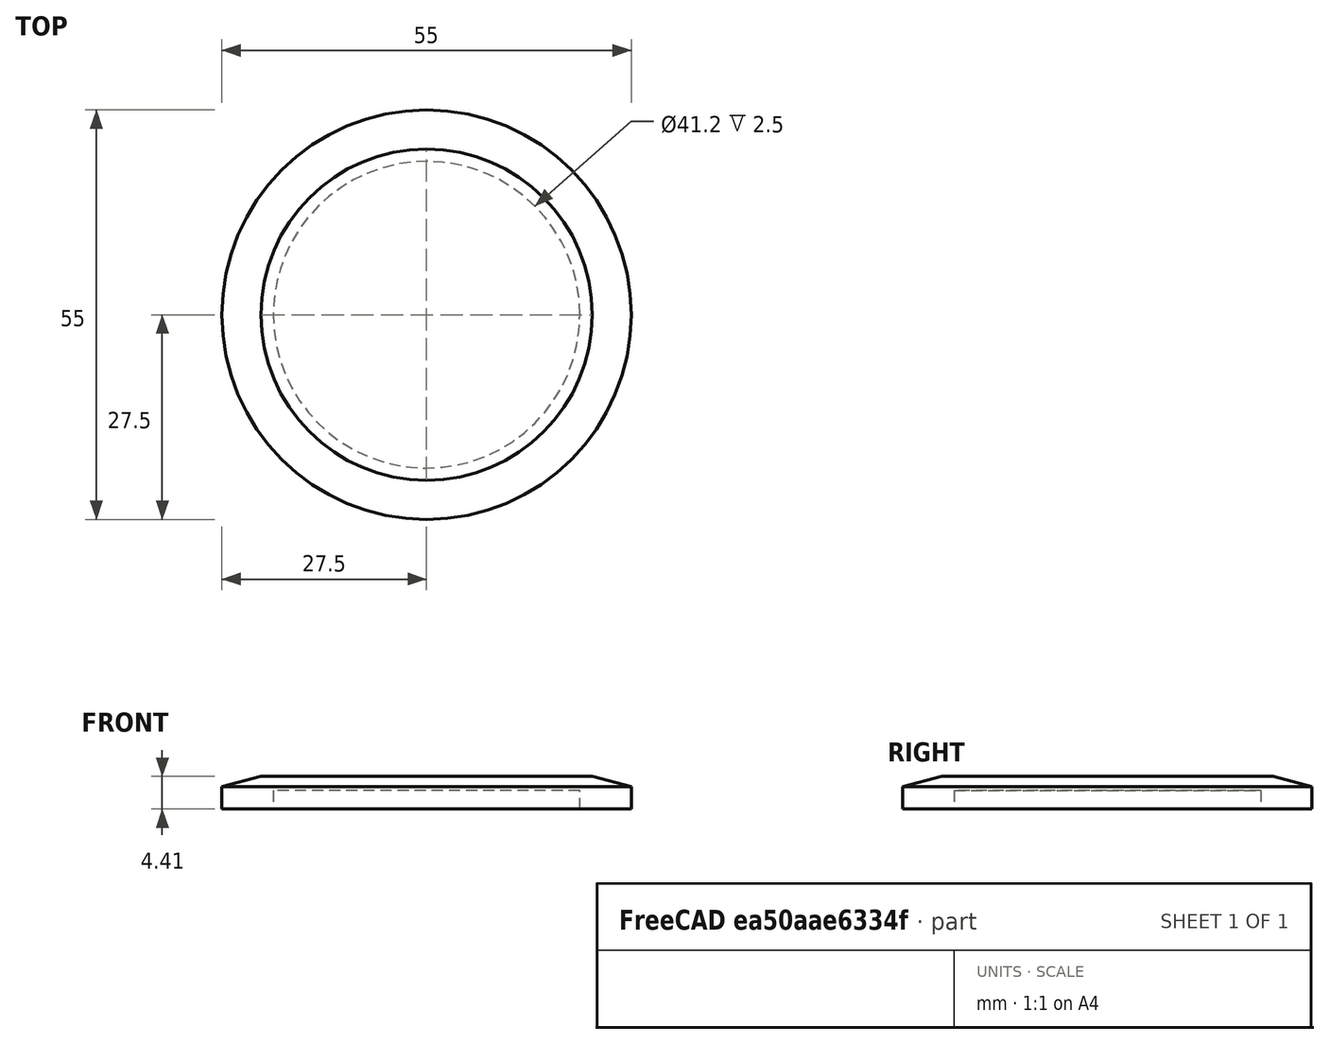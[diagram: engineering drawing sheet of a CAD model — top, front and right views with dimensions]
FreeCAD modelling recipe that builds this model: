
FCSTD DOCUMENT  (FreeCAD 1.0R1.0.0)
Label: KFBlank
License: All rights reserved
LicenseURL: http://en.wikipedia.org/wiki/All_rights_reserved
objects: Part::Cylinder×2, Part::Cone×1, Part::MultiFuse×1, Spreadsheet::Sheet×1, Part::Cut×1
note: 5 computed .brp shape members not serialized (recipe doc carries the construction recipe); baked Part::Feature solids carry a one-line shape summary decoded from their .brp

FEATURE [Part::Cone] Cone
  Angle = 360
  AttacherType = Attacher::AttachEngine3D
  Height = 1.40673
  Placement = pos=(0,0,3) rot=(0,0,1;0rad)
  Radius1 = 27.5
  Radius2 = 22.25
  expr: Height = <<KleinFlange>>.coupling_taper_height
  expr: Radius1 = <<KleinFlange>>.d3 / 2
  expr: Radius2 = <<KleinFlange>>.d1 / 2
FEATURE [Part::Cylinder] Cylinder
  Angle = 360
  AttacherType = Attacher::AttachEngine3D
  FirstAngle = 0
  Height = 3
  Radius = 27.5
  SecondAngle = 0
  expr: Radius = <<KleinFlange>>.d3 / 2
FEATURE [Part::Cylinder] Cylinder002
  Angle = 360
  AttacherType = Attacher::AttachEngine3D
  FirstAngle = 0
  Height = 2.5
  Radius = 20.6
  SecondAngle = 0
  expr: Height = <<KleinFlange>>.oring_recess
  expr: Radius = <<KleinFlange>>.d2 / 2
FEATURE [Part::MultiFuse] Fusion
  Shapes = -> [Cylinder,Cone]
FEATURE [Spreadsheet::Sheet] Spreadsheet  label="KleinFlange"
  KF = 3
  cells = A1='Nominal bore; B1='D: O-ring ID; C1='d1: Pipe OD; D1='d2: Carrier retainer diameter; E1='d3: Coupling OD; F1='d4: Carrier ID; G1='d5: Connecting Pipe Carrier OD; H1='d6: OD to hold Oring in carrier; I1='R: O ring retainer radius (carrier); A2==hiddenref(.KF.String); B2(D)==.B6; C2(d1)==.C6; D2(d2)==.D6; E2(d3)==.E6; F2(d4)==.F6; G2(d5)==.G6; H2(d6)==.H6; I2(R)=; A3='10; B3=15; C3=14; D3=12.2; E3=30; F3=10; G3=12; H3=15.3; A4='16; B4=18; C4=20; D4=17.2; E4=30; F4=16; G4=17; H4=18.5; A5='25; B5=28; C5=28; D5=26.2; E5=40; F5=25; G5=26; H5=28.5; A6='40; B6=42; C6=44.5; D6=41.2; E6=55; F6=40; G6=41; H6=43; A7='50; B7=55; C7=61; D7=52.2; E7=75; F7=50; G7=52; H7=55.5; A9='O Ring; A10='O ring diameter; B10(oring_dia)=5; A11='Inner diameter; B11==B2; A13='Coupling; L13='Coupling calculated properties; A14='Total length; B14(coupling_len)=10; C14='10 is minimum length; L14='Taper height; M14(coupling_taper_height)==(d3 - d1) / (2 * tan(90 - 15)); A15='Pipe diameter; B15(pipe_dia_user)=100; C15='Maximum specified by d5 (Connecting pipe diameter); L15='Effective pipe diameter; M15(coupling_pipe_ID)==min(d5; pipe_dia_user); L16='Effective coupling length; M16(coupling_len_eff)==min(coupling_len; 10); A17='O Ring carrier interface; A18='O ring carrier recess; B18(oring_recess)=2.5; C18='>= 2.5 by norm
  expr: .KF.Enum = cells[<<A3:|>>]
  expr: .cells.Bind.B2.I2 = tuple(.cells; <<B>> + str(hiddenref(KF) + 3); <<I>> + str(hiddenref(KF) + 3))
FEATURE [Part::Cut] Cut  label="KFBlank"
  Base = -> Fusion
  Tool = -> Cylinder002
